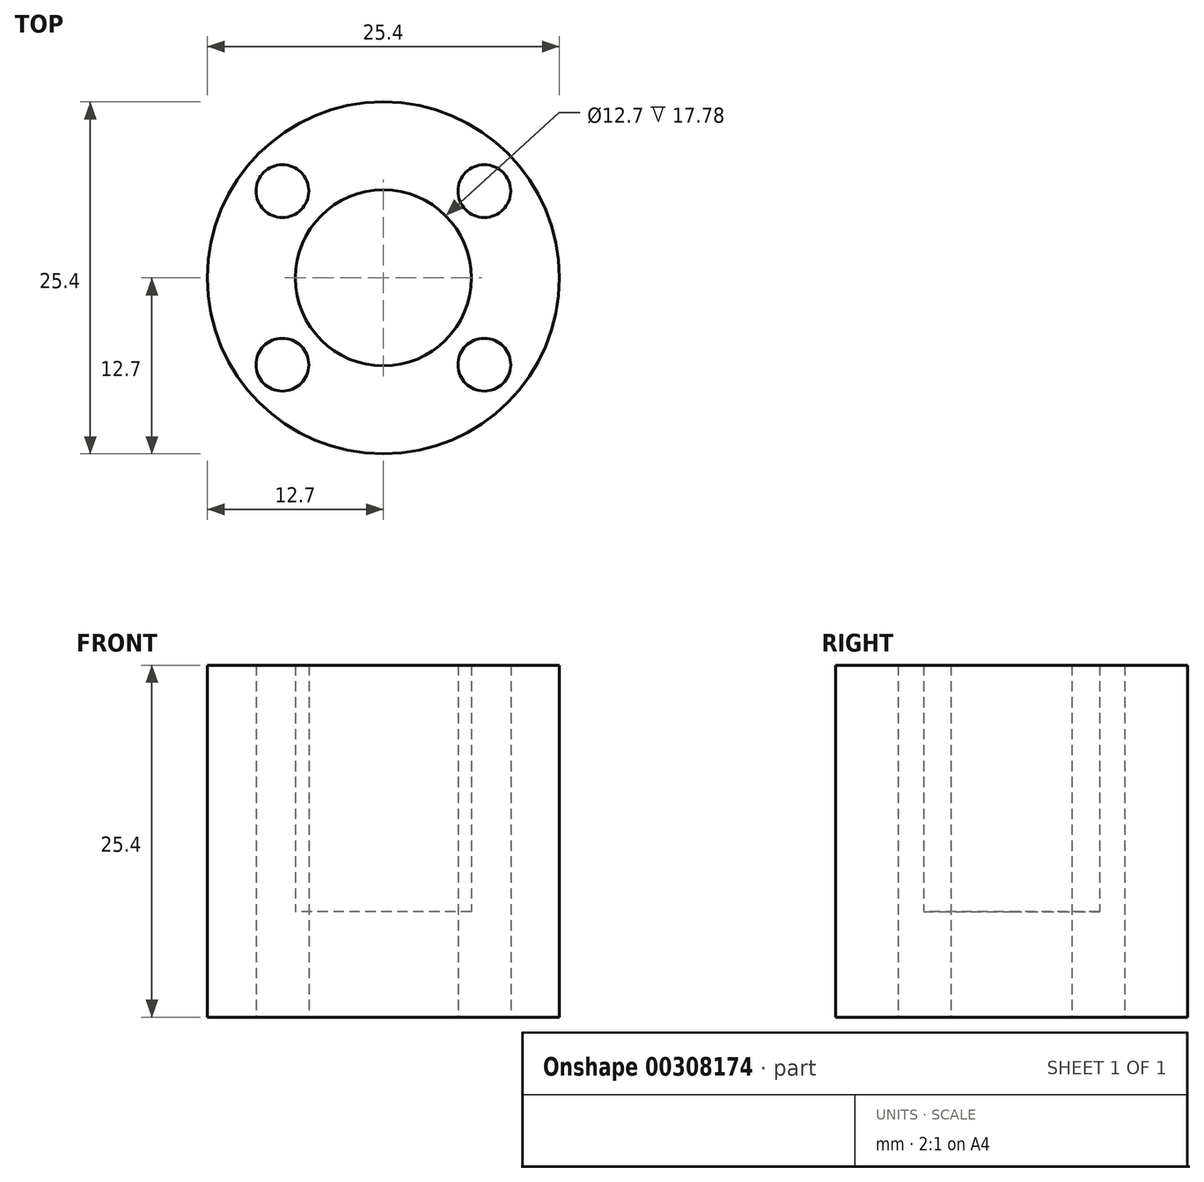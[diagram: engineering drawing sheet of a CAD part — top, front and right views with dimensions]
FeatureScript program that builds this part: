
annotation { "Feature Type Name" : "Feature", "Feature Type Description" : "" }
export const myFeature = defineFeature(function(context is Context, id is Id, definition is map)
    precondition{}
    {
        {
            var Q0;
            Q0=qCreatedBy(makeId("Top.planeOp"),FACE);
            var sketch = newSketch(context, id + "F0", { "sketchPlane" : qUnion([Q0])});
            skCircle(sketch, "E0", {"center": v(0, 0) * mm, "radius": 12.7 * mm});
            skCircle(sketch, "E1", {"center": v(0, 0) * mm, "radius": 6.35 * mm});
            skCircle(sketch, "E2", {"center": v(0, 0) * mm, "radius": 4 * mm});
            skCircle(sketch, "E3", {"center": v(-7.29, 6.27) * mm, "radius": 1.9 * mm});
            skCircle(sketch, "E4", {"center": v(7.29, 6.27) * mm, "radius": 1.9 * mm});
            skCircle(sketch, "E5", {"center": v(-7.29, -6.27) * mm, "radius": 1.9 * mm});
            skCircle(sketch, "E6", {"center": v(7.29, -6.27) * mm, "radius": 1.9 * mm});
            skSolve(sketch);
        }
        {
            var Q0;
            Q0=makeQuery(id+"F0.imprint","IMPRINT",FACE,{"disambiguationData":[TD([[makeQuery(id+"F0.imprint","IMPRINT",EDGE,{"derivedFrom":sQuery(id+"F0.wireOp",EDGE,"E0")}),1.0]])]});
            extrude(context, id + "F1", {"entities" : qUnion([Q0]), "depth" : 25.4 * mm});
        }
        {
            var Q0;
            Q0=makeQuery(id+"F0.imprint","IMPRINT",FACE,{"disambiguationData":[TD([[makeQuery(id+"F0.imprint","IMPRINT",EDGE,{"derivedFrom":sQuery(id+"F0.wireOp",EDGE,"E1")}),1.0]])]});
            extrude(context, id + "F2", {"entities" : qUnion([Q0]), "operationType" : NewBodyOperationType.ADD, "depth" : 7.62 * mm});
        }
        {
            var Q0;
            Q0=makeQuery(id+"F0.imprint","IMPRINT",FACE,{"disambiguationData":[TD([[makeQuery(id+"F0.imprint","IMPRINT",EDGE,{"derivedFrom":sQuery(id+"F0.wireOp",EDGE,"E2")}),1.0]])]});
            extrude(context, id + "F3", {"entities" : qUnion([Q0]), "operationType" : NewBodyOperationType.ADD, "depth" : 7.62 * mm});
        }
    });
